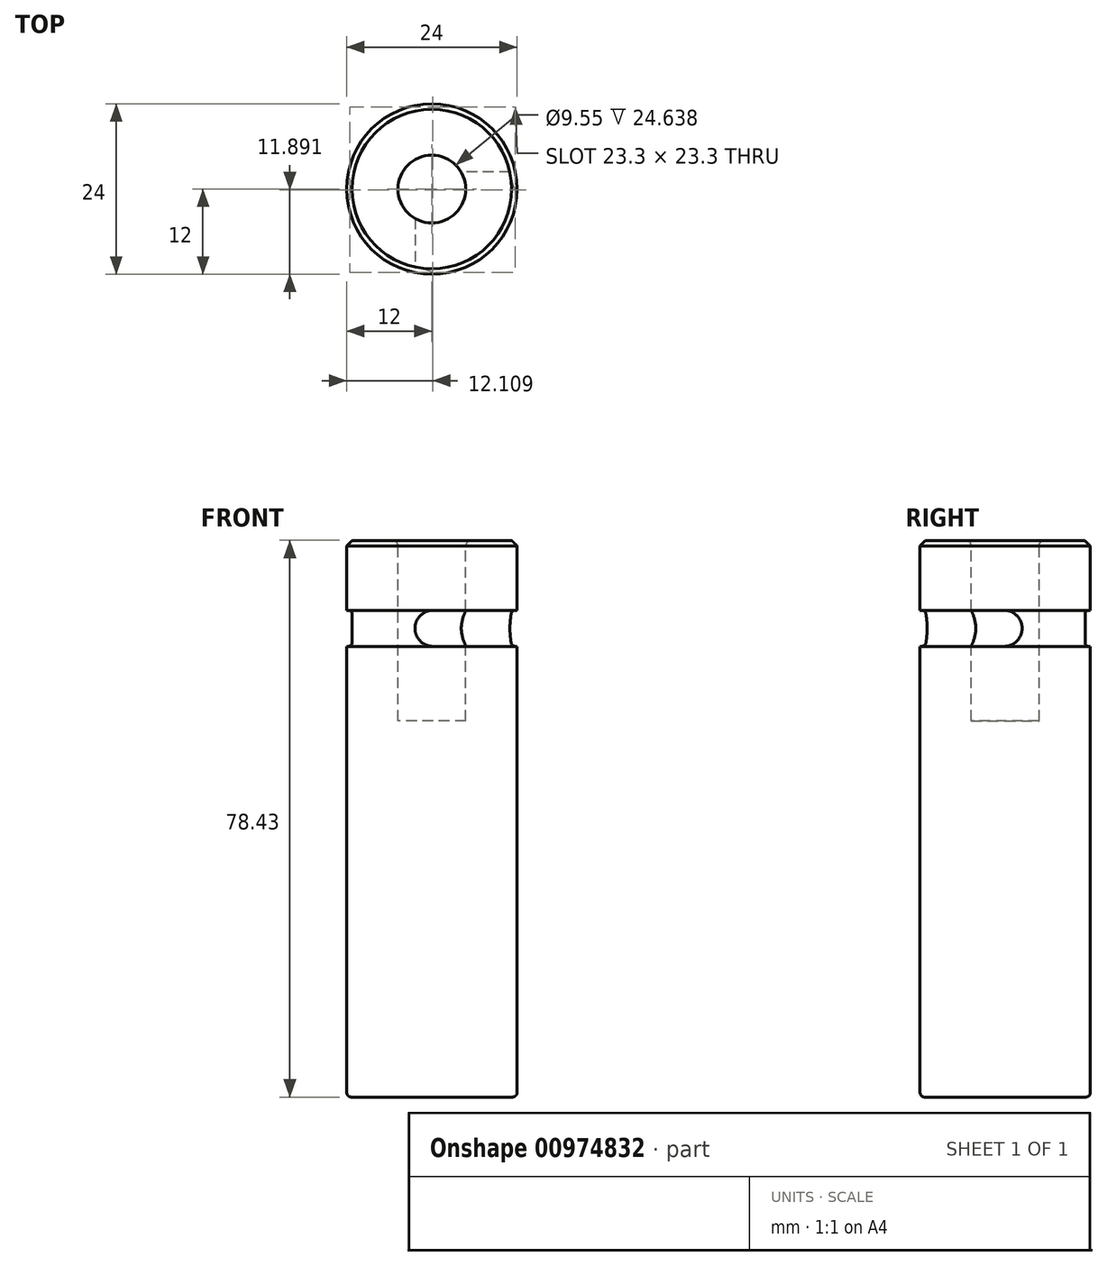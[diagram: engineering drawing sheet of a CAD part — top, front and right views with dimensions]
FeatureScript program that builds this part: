
annotation { "Feature Type Name" : "Feature", "Feature Type Description" : "" }
export const myFeature = defineFeature(function(context is Context, id is Id, definition is map)
    precondition{}
    {
        {
            var Q0;
            Q0=qCreatedBy(makeId("Front.planeOp"),FACE);
            var sketch = newSketch(context, id + "F0", { "sketchPlane" : qUnion([Q0])});
            skLineSegment(sketch, "E0", {"start": v(0, -40.04) * mm, "end": v(11.36, -40.04) * mm});
            skLineSegment(sketch, "E1", {"start": v(12, -39.4) * mm, "end": v(12, 23.46) * mm});
            skLineSegment(sketch, "E2", {"start": v(12, 23.46) * mm, "end": v(11.25, 23.46) * mm});
            skLineSegment(sketch, "E3", {"start": v(11.25, 23.46) * mm, "end": v(11.25, 28.54) * mm});
            skLineSegment(sketch, "E4", {"start": v(11.25, 28.54) * mm, "end": v(12, 28.54) * mm});
            skLineSegment(sketch, "E5", {"start": v(12, 28.54) * mm, "end": v(12, 37.62) * mm});
            skLineSegment(sketch, "E6", {"start": v(11.24, 38.39) * mm, "end": v(5.54, 38.39) * mm});
            skLineSegment(sketch, "E7", {"start": v(4.78, 37.62) * mm, "end": v(4.78, 12.99) * mm});
            skLineSegment(sketch, "E8", {"start": v(4.78, 12.99) * mm, "end": v(0, 12.99) * mm});
            skLineSegment(sketch, "E9", {"start": v(0, 12.99) * mm, "end": v(0, -40.04) * mm});
            skPoint(sketch, "E10.visualSharp", {"position": v(4.78, 38.39) * mm});
            skArc(sketch, "E10.filletArc", {"start": v(5.54, 38.39) * mm, "mid": v(5, 38.16) * mm, "end": v(4.78, 37.62) * mm});
            skPoint(sketch, "E11.visualSharp", {"position": v(12, 38.39) * mm});
            skLineSegment(sketch, "E12", {"start": v(11.24, 38.39) * mm, "end": v(12, 37.62) * mm});
            skPoint(sketch, "E13.visualSharp", {"position": v(12, -40.04) * mm});
            skArc(sketch, "E13.filletArc", {"start": v(11.36, -40.04) * mm, "mid": v(11.81, -39.85) * mm, "end": v(12, -39.4) * mm});
            skSolve(sketch);
        }
        {
            var Q0;
            Q0=makeQuery(id+"F0.imprint","IMPRINT",FACE,{"disambiguationData":[TD([[makeQuery(id+"F0.imprint","IMPRINT",EDGE,{"derivedFrom":sQuery(id+"F0.wireOp",EDGE,"E0")}),1.0]])]});
            var Q1;
            Q1=sQuery(id+"F0.wireOp",EDGE,"E9");
            revolve(context, id + "F1", {"surfaceOperationType" : NewSurfaceOperationType.NEW, "entities" : qUnion([Q0]), "axis" : qUnion([Q1]), "revolveType" : RevolveType.FULL});
        }
        {
            var Q0;
            Q0=makeQuery(id+"F1.opRevolve","SWEPT_FACE",FACE,{"disambiguationData":[OSD([sQuery(id+"F0.wireOp",EDGE,"E2")])]});
            var sketch = newSketch(context, id + "F2", { "sketchPlane" : qUnion([Q0])});
            skLineSegment(sketch, "E14", {"start": v(-2.38, 0) * mm, "end": v(-2.38, -24.26) * mm});
            skLineSegment(sketch, "E15", {"start": v(-2.38, 2.38) * mm, "end": v(24.37, 2.38) * mm});
            skLineSegment(sketch, "E16", {"start": v(24.37, 2.38) * mm, "end": v(-2.38, -24.26) * mm});
            skLineSegment(sketch, "E17", {"start": v(-2.38, 0) * mm, "end": v(-2.38, 2.38) * mm});
            skSolve(sketch);
        }
        {
            var Q0;
            {var subQ0=sQuery(id+"F2.wireOp",EDGE,"E17");Q0=makeQuery(id+"F2.imprint","IMPRINT",FACE,{"disambiguationData":[TD([[makeQuery(id+"F2.imprint","IMPRINT",EDGE,{"derivedFrom":subQ0}),-1.0]])]});}
            extrude(context, id + "F3", {"entities" : qUnion([Q0]), "operationType" : NewBodyOperationType.REMOVE, "depth" : 5.08 * mm, "offsetDistance" : 25.4 * mm});
        }
        {
            var Q0;
            Q0=makeQuery(id+"F3.boolean.opBoolean","COPY",EDGE,{"derivedFrom":makeQuery(id+"F3.opExtrude","CAP_EDGE",EDGE,{"disambiguationData":[OSD([sQuery(id+"F2.wireOp",EDGE,"E14"),sQuery(id+"F2.wireOp",EDGE,"E17")])],"isStart":true})});
            var Q1;
            Q1=makeQuery(id+"F3.boolean.opBoolean","COPY",EDGE,{"derivedFrom":makeQuery(id+"F3.opExtrude","CAP_EDGE",EDGE,{"disambiguationData":[OSD([sQuery(id+"F2.wireOp",EDGE,"E15")])],"isStart":true})});
            var Q2;
            Q2=makeQuery(id+"F3.boolean.opBoolean","COPY",EDGE,{"derivedFrom":makeQuery(id+"F3.opExtrude","CAP_EDGE",EDGE,{"disambiguationData":[OSD([sQuery(id+"F2.wireOp",EDGE,"E14"),sQuery(id+"F2.wireOp",EDGE,"E17")])],"isStart":false})});
            var Q3;
            Q3=makeQuery(id+"F3.boolean.opBoolean","COPY",EDGE,{"derivedFrom":makeQuery(id+"F3.opExtrude","CAP_EDGE",EDGE,{"disambiguationData":[OSD([sQuery(id+"F2.wireOp",EDGE,"E15")])],"isStart":false})});
            fillet(context, id + "F4", {"entities" : qUnion([Q0, Q1, Q2, Q3]), "radius" : 2.54 * mm, "tangentPropagation" : true, "allowEdgeOverflow" : false});
        }
        {
            var Q0;
            Q0=makeQuery(id+"F1.opRevolve","SWEPT_EDGE",EDGE,{"disambiguationData":[OSD([sQuery(id+"F0.wireOp",EDGE,"E3"),sQuery(id+"F0.wireOp",EDGE,"E4")])]});
            var Q1;
            Q1=makeQuery(id+"F1.opRevolve","SWEPT_EDGE",EDGE,{"disambiguationData":[OSD([sQuery(id+"F0.wireOp",EDGE,"E2"),sQuery(id+"F0.wireOp",EDGE,"E3")])]});
            fillet(context, id + "F5", {"entities" : qUnion([Q0, Q1]), "radius" : 0.5 * mm, "tangentPropagation" : true, "allowEdgeOverflow" : false});
        }
    });
